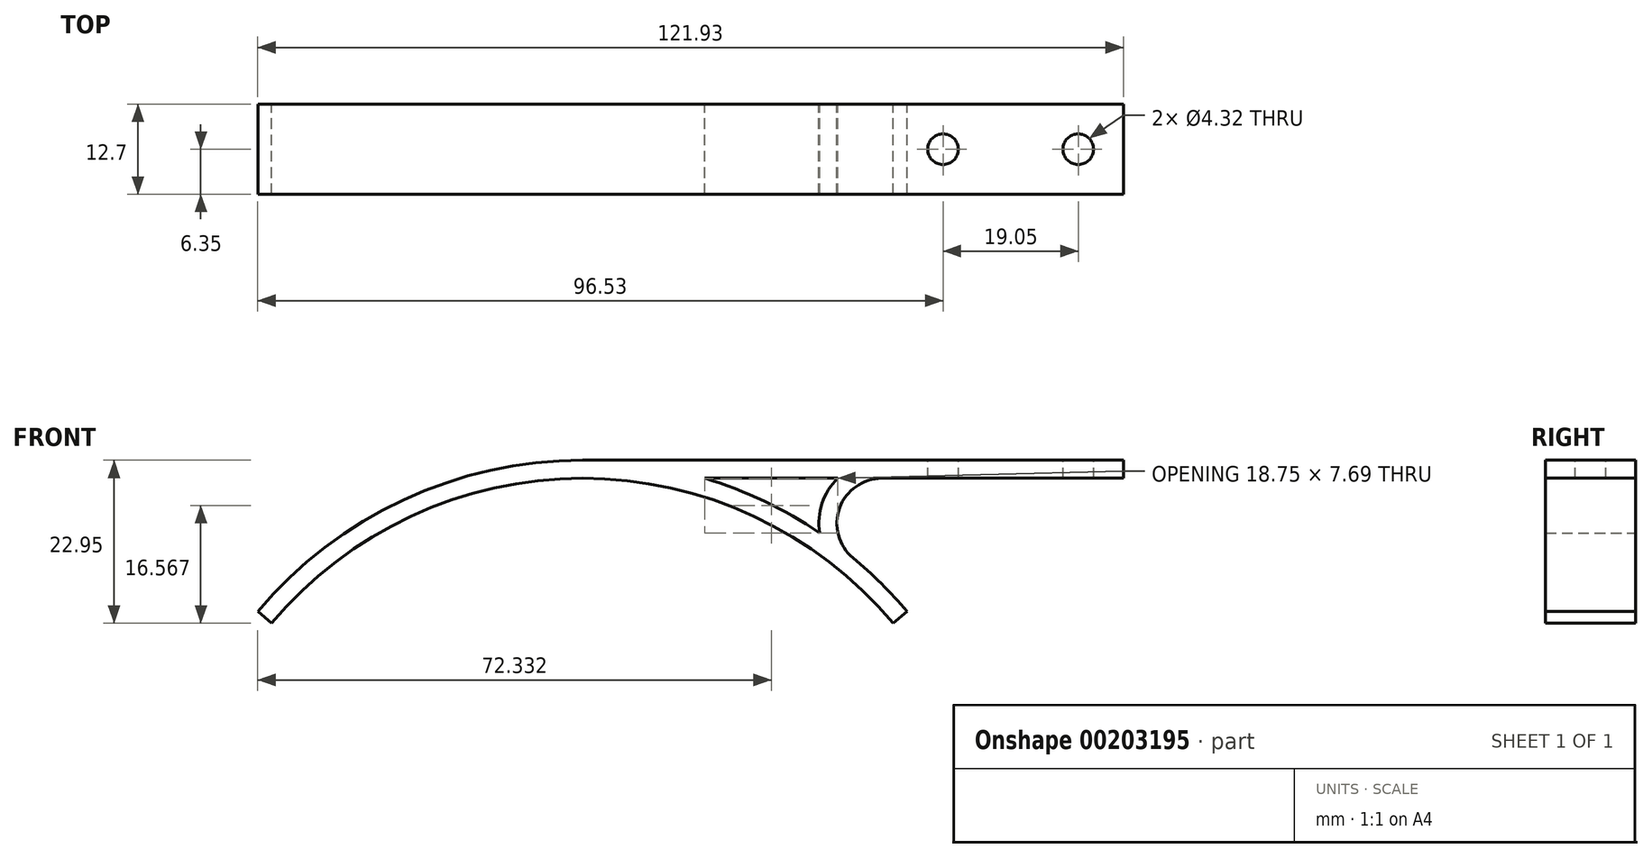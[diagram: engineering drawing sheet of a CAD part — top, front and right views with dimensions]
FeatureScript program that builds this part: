
annotation { "Feature Type Name" : "Feature", "Feature Type Description" : "" }
export const myFeature = defineFeature(function(context is Context, id is Id, definition is map)
    precondition{}
    {
        {
            var Q0;
            Q0=qCreatedBy(makeId("Front.planeOp"),FACE);
            var sketch = newSketch(context, id + "F0", { "sketchPlane" : qUnion([Q0])});
            skArc(sketch, "E0", {"start": v(43.78, 36.74) * mm, "mid": v(0, 57.15) * mm, "end": v(-43.78, 36.74) * mm});
            skArc(sketch, "E1.0", {"start": v(0, 59.7) * mm, "mid": v(-25.23, 54.1) * mm, "end": v(-45.73, 38.37) * mm});
            skLineSegment(sketch, "E2", {"start": v(0, 0) * mm, "end": v(0, 57.15) * mm});
            skLineSegment(sketch, "E3", {"start": v(0, 59.7) * mm, "end": v(76.2, 59.7) * mm});
            skLineSegment(sketch, "E4", {"start": v(76.2, 59.7) * mm, "end": v(76.2, 57.15) * mm});
            skLineSegment(sketch, "E5", {"start": v(76.2, 57.15) * mm, "end": v(42.2, 57.15) * mm});
            skArc(sketch, "E6", {"start": v(42.2, 57.15) * mm, "mid": v(36.23, 52.96) * mm, "end": v(38.14, 45.92) * mm});
            skArc(sketch, "E7.0", {"start": v(35.98, 57.15) * mm, "mid": v(33.77, 53.62) * mm, "end": v(33.4, 49.46) * mm});
            skArc(sketch, "E8.trimOffspring", {"start": v(33.4, 49.46) * mm, "mid": v(25.6, 53.92) * mm, "end": v(17.23, 57.15) * mm});
            skLineSegment(sketch, "E9.trimOffspring", {"start": v(35.98, 57.15) * mm, "end": v(17.23, 57.15) * mm});
            skLineSegment(sketch, "E10", {"start": v(-43.78, 36.74) * mm, "end": v(-45.73, 38.37) * mm});
            skLineSegment(sketch, "E11.MirrorCS", {"start": v(43.78, 36.74) * mm, "end": v(45.73, 38.37) * mm});
            skArc(sketch, "E12.trimOffspring", {"start": v(45.73, 38.37) * mm, "mid": v(42.1, 42.31) * mm, "end": v(38.14, 45.92) * mm});
            skSolve(sketch);
        }
        {
            var Q0;
            Q0=makeQuery(id+"F0.imprint","IMPRINT",FACE,{"disambiguationData":[TD([[makeQuery(id+"F0.imprint","IMPRINT",EDGE,{"derivedFrom":sQuery(id+"F0.wireOp",EDGE,"E1.0")}),1.0]])]});
            extrude(context, id + "F1", {"entities" : qUnion([Q0]), "depth" : 12.7 * mm});
        }
        {
            var Q0;
            Q0=makeQuery(id+"F1.opExtrude","SWEPT_FACE",FACE,{"disambiguationData":[OSD([sQuery(id+"F0.wireOp",EDGE,"E5")])]});
            var sketch = newSketch(context, id + "F2", { "sketchPlane" : qUnion([Q0])});
            skLineSegment(sketch, "E13", {"start": v(76.2, 6.35) * mm, "end": v(50.8, 6.35) * mm});
            skPoint(sketch, "E13.endSnap0", {"position": v(76.2, 6.35) * mm});
            skLineSegment(sketch, "E14", {"start": v(50.8, 6.35) * mm, "end": v(69.85, 6.35) * mm});
            skSolve(sketch);
        }
        {
            var Q0;
            Q0=sQuery(id+"F2.wireOp",VERTEX,"E14.end");
            var Q1;
            Q1=sQuery(id+"F2.wireOp",VERTEX,"E13.end");
            var Q2;
            Q2=makeQuery(id+"F1.opExtrude","SWEPT_BODY",BODY,{"disambiguationData":[OSD([sQuery(id+"F0.wireOp",EDGE,"E0"),sQuery(id+"F0.wireOp",EDGE,"E1.0"),sQuery(id+"F0.wireOp",EDGE,"E3"),sQuery(id+"F0.wireOp",EDGE,"E4"),sQuery(id+"F0.wireOp",EDGE,"E5"),sQuery(id+"F0.wireOp",EDGE,"E6"),sQuery(id+"F0.wireOp",EDGE,"E7.0"),sQuery(id+"F0.wireOp",EDGE,"E8.trimOffspring"),sQuery(id+"F0.wireOp",EDGE,"E9.trimOffspring"),sQuery(id+"F0.wireOp",EDGE,"E10"),sQuery(id+"F0.wireOp",EDGE,"E11.MirrorCS"),sQuery(id+"F0.wireOp",EDGE,"E12.trimOffspring")])]});
            hole(context, id + "F3", {"style" : HoleStyle.SIMPLE, "endStyle" : HoleEndStyle.BLIND, "standardTappedOrClearance" : lookupTablePath({ "standard" : "ANSI", "fit" : "Close", "size" : "#8", "type" : "Clearance" }), "standardBlindInLast" : lookupTablePath({ "fit" : "Close", "standard" : "ANSI", "size" : "#8", "type" : "Clearance" }), "holeDiameter" : 4.32 * mm, "holeDepth" : 25.4 * mm, "locations" : qUnion([Q0, Q1]), "scope" : qUnion([Q2])});
        }
    });
